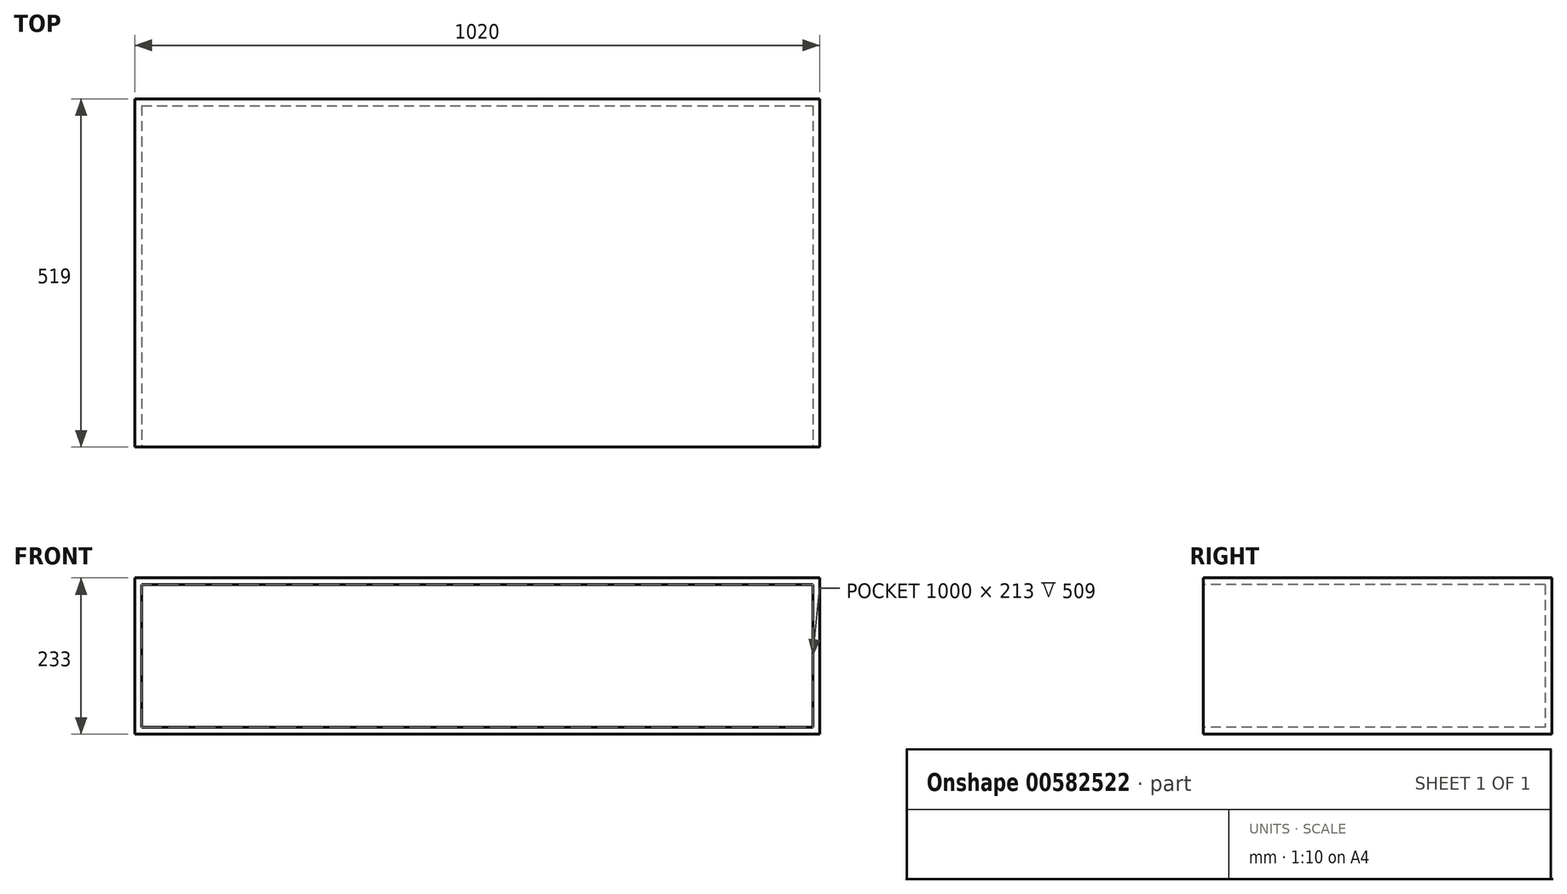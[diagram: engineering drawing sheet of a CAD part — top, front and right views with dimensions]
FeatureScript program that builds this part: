
annotation { "Feature Type Name" : "Feature", "Feature Type Description" : "" }
export const myFeature = defineFeature(function(context is Context, id is Id, definition is map)
    precondition{}
    {
        {
            var Q0;
            Q0=qCreatedBy(makeId("Front.planeOp"),FACE);
            var sketch = newSketch(context, id + "F0", { "sketchPlane" : qUnion([Q0])});
            skLineSegment(sketch, "E0.bottom", {"start": v(-500, 213) * mm, "end": v(500, 213) * mm});
            skLineSegment(sketch, "E0.top", {"start": v(-500, 0) * mm, "end": v(500, 0) * mm});
            skLineSegment(sketch, "E0.left", {"start": v(-500, 213) * mm, "end": v(-500, 0) * mm});
            skLineSegment(sketch, "E0.right", {"start": v(500, 213) * mm, "end": v(500, 0) * mm});
            skLineSegment(sketch, "E1.0", {"start": v(510, 223) * mm, "end": v(510, -10) * mm});
            skLineSegment(sketch, "E1.1", {"start": v(-510, 223) * mm, "end": v(510, 223) * mm});
            skLineSegment(sketch, "E1.2", {"start": v(-510, 223) * mm, "end": v(-510, -10) * mm});
            skLineSegment(sketch, "E1.3", {"start": v(-510, -10) * mm, "end": v(510, -10) * mm});
            skSolve(sketch);
        }
        {
            var Q0;
            Q0 = qSketchRegion(id + "F0", true);
            extrude(context, id + "F1", {"entities" : qUnion([Q0]), "oppositeDirection" : true, "depth" : 509 * mm, "offsetDistance" : 25 * mm});
        }
        {
            var Q0;
            Q0=makeQuery(id+"F1.opExtrude","CAP_FACE",FACE,{"disambiguationData":[OSD([sQuery(id+"F0.wireOp",EDGE,"E0.bottom"),sQuery(id+"F0.wireOp",EDGE,"E0.top"),sQuery(id+"F0.wireOp",EDGE,"E0.left"),sQuery(id+"F0.wireOp",EDGE,"E0.right"),sQuery(id+"F0.wireOp",EDGE,"E1.0"),sQuery(id+"F0.wireOp",EDGE,"E1.1"),sQuery(id+"F0.wireOp",EDGE,"E1.2"),sQuery(id+"F0.wireOp",EDGE,"E1.3")])],"isStart":false});
            var sketch = newSketch(context, id + "F2", { "sketchPlane" : qUnion([Q0])});
            skSolve(sketch);
        }
        {
            var Q0;
            Q0 = qSketchRegion(id + "F2", true);
            var Q1;
            Q1=makeQuery(id+"F2.imprint","IMPRINT",FACE,{"disambiguationData":[TD([[makeQuery(id+"F2.imprint","IMPRINT",EDGE,{"derivedFrom":makeQuery(id+"F1.opExtrude","CAP_EDGE",EDGE,{"disambiguationData":[OSD([sQuery(id+"F0.wireOp",EDGE,"E0.bottom")])],"isStart":false})}),-1.0]])]});
            var Q2;
            Q2=makeQuery(id+"F2.imprint","IMPRINT",FACE,{"disambiguationData":[TD([[makeQuery(id+"F2.imprint","IMPRINT",EDGE,{"derivedFrom":makeQuery(id+"F1.opExtrude","CAP_EDGE",EDGE,{"disambiguationData":[OSD([sQuery(id+"F0.wireOp",EDGE,"E0.bottom")])],"isStart":false})}),1.0]])]});
            extrude(context, id + "F3", {"entities" : qUnion([Q0, Q1, Q2]), "operationType" : NewBodyOperationType.ADD, "depth" : 10 * mm, "offsetDistance" : 25 * mm});
        }
    });
